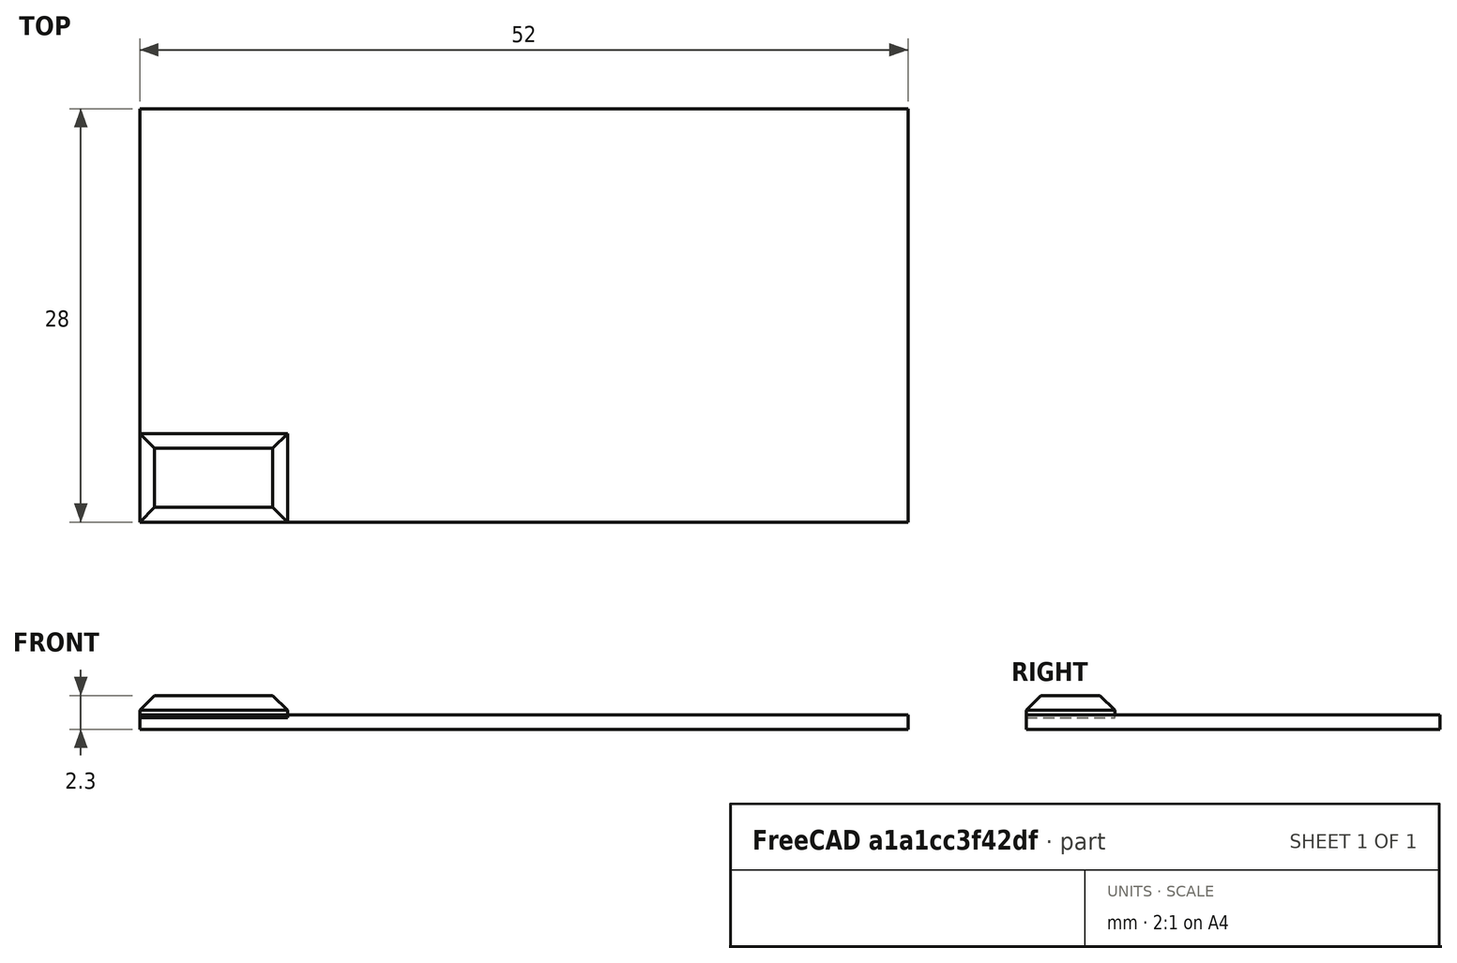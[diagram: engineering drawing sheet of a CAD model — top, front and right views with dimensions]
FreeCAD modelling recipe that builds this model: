
FCSTD DOCUMENT  (FreeCAD 1.0R39319 (Git))
Label: ojt1_t12r02_chocolat
License: All rights reserved
LicenseURL: https://en.wikipedia.org/wiki/All_rights_reserved
objects: Part::Chamfer×4, Part::Box×2, Part::FeaturePython×1
note: 6 computed .brp shape members not serialized (recipe doc carries the construction recipe); baked Part::Feature solids carry a one-line shape summary decoded from their .brp

FEATURE [Part::Box] Box  label="Cub"
  AttacherType = Attacher::AttachEngine3D
  Height = 1
  Length = 52
  Placement = pos=(0,0,0.2) rot=(0,0,1;0rad)
  Width = 28
FEATURE [Part::Box] Box001  label="Cub001"
  AttacherType = Attacher::AttachEngine3D
  Height = 1.5
  Length = 10
  Placement = pos=(0,0,1) rot=(0,0,1;0rad)
  Width = 6
FEATURE [Part::Chamfer] Chamfer
  Base = -> Box001
  EdgeLinks = -> Box001 [Edge10]
  Edges = 1 edges r=1: [Edge10]
FEATURE [Part::Chamfer] Chamfer001
  Base = -> Chamfer
  EdgeLinks = -> Chamfer [Edge14]
  Edges = 1 edges r=1: [Edge14]
FEATURE [Part::Chamfer] Chamfer002
  Base = -> Chamfer001
  EdgeLinks = -> Chamfer001 [Edge6]
  Edges = 1 edges r=1: [Edge6]
FEATURE [Part::Chamfer] Chamfer003
  Base = -> Chamfer002
  EdgeLinks = -> Chamfer002 [Edge7]
  Edges = 1 edges r=1: [Edge7]
FEATURE [Part::FeaturePython] Array  # Draft array (typed FeaturePython)
  AlwaysSyncPlacement = false
  Angle = 360
  ArrayType = 0
  Axis = (0,0,1)
  Base = -> Chamfer003
  Center = (0,0,0)
  Count = 25
  ExpandArray = false
  Fuse = false
  IntervalAxis = (0,0,0)
  IntervalX = (10.5,0,0)
  IntervalY = (0,5.5,0)
  IntervalZ = (0,0,100)
  NumberCircles = 3
  NumberPolar = 5
  NumberX = 5
  NumberY = 5
  NumberZ = 1
  PlacementList = 25 placements: [(0,0,0),(0,5.5,0),(0,11,0),(0,16.5,0),(0,22,0),(10.5,0,0),(10.5,5.5,0),(10.5,11,0),(10.5,16.5,0),(10.5,22,0),(21,0,0),(21,5.5,0),(21,11,0),(21,16.5,0),(21,22,0),(31.5,0,0),(31.5,5.5,0),(31.5,11,0),(31.5,16.5,0),(31.5,22,0),(42,0,0),(42,5.5,0),(42,11,0),(42,16.5,0),(42,22,0)]
  RadialDistance = 50
  ScaleList = (25) [(1,1,1),(1,1,1),(1,1,1),(1,1,1),(1,1,1),(1,1,1),(1,1,1),(1,1,1),(1,1,1),(1,1,1),(1,1,1),(1,1,1),(1,1,1),(1,1,1),(1,1,1),(1,1,1),(1,1,1),(1,1,1),+7 more]
  Symmetry = 1
  TangentialDistance = 25
